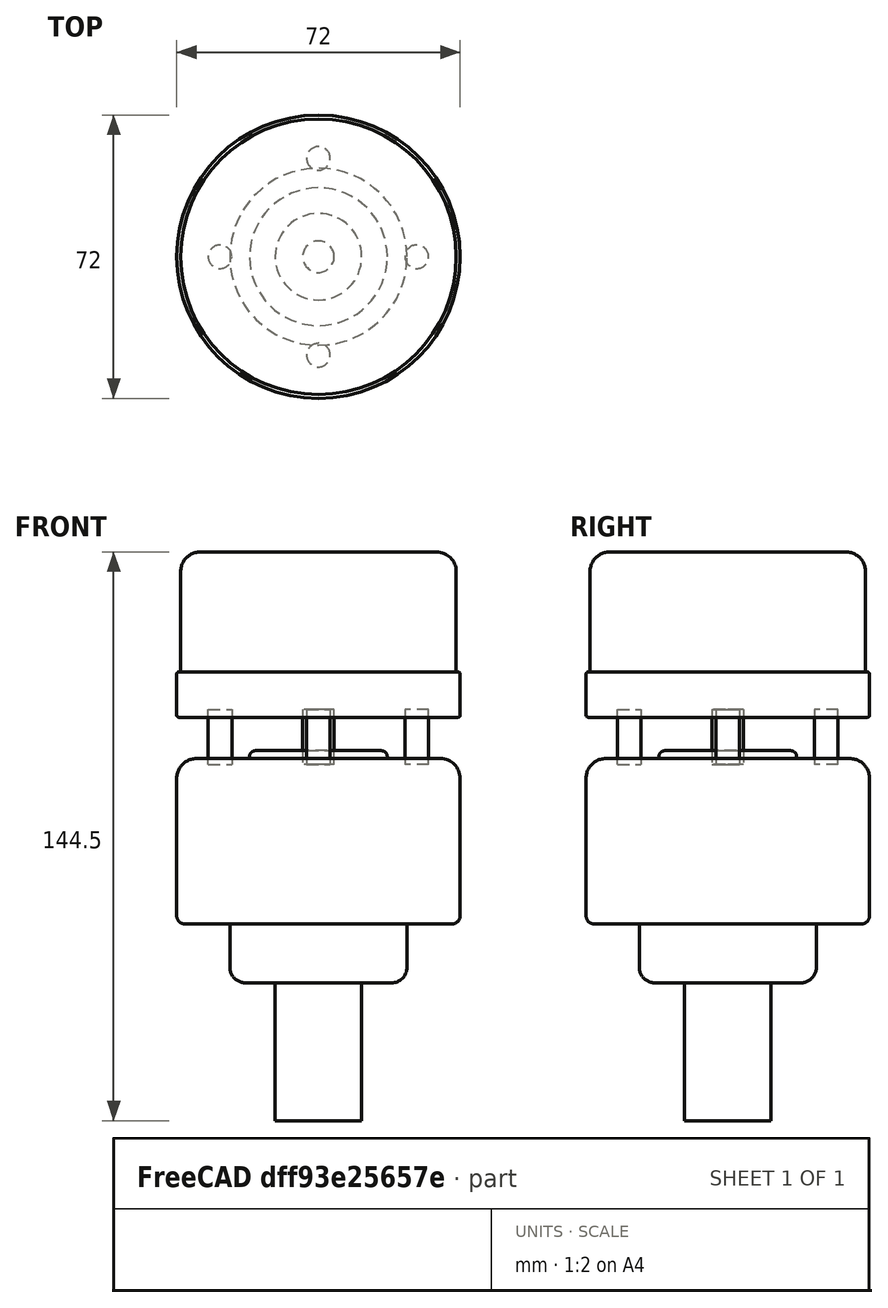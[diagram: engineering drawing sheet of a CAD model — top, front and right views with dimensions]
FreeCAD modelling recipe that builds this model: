
FCSTD DOCUMENT  (FreeCAD 0.21R33668 +7 (Git))
Label: Airmar
License: All rights reserved
LicenseURL: https://en.wikipedia.org/wiki/All_rights_reserved
objects: Part::Cylinder×16, Part::MultiFuse×8, Part::Fillet×5, Part::Mirroring×4, Part::Cut×1
note: 34 computed .brp shape members not serialized (recipe doc carries the construction recipe); baked Part::Feature solids carry a one-line shape summary decoded from their .brp

FEATURE [Part::Cylinder] Cylinder  label="Upper"
  Angle = 360
  AttacherType = Attacher::AttachEngine3D
  FirstAngle = 0
  Height = 42
  Radius = 35
  SecondAngle = 0
FEATURE [Part::Cylinder] Cylinder001  label="Lower"
  Angle = 360
  AttacherType = Attacher::AttachEngine3D
  FirstAngle = 0
  Height = 42
  Placement = pos=(0,0,-52.5) rot=(0,0,1;0rad)
  Radius = 36
  SecondAngle = 0
FEATURE [Part::Cylinder] Cylinder002  label="Cap"
  Angle = 360
  AttacherType = Attacher::AttachEngine3D
  FirstAngle = 0
  Height = 15
  Placement = pos=(0,0,-67.5) rot=(0,0,1;0rad)
  Radius = 22.5
  SecondAngle = 0
FEATURE [Part::Cylinder] Cylinder003  label="Mount"
  Angle = 360
  AttacherType = Attacher::AttachEngine3D
  FirstAngle = 0
  Height = 35
  Placement = pos=(0,0,-102.5) rot=(0,0,1;0rad)
  Radius = 11
  SecondAngle = 0
FEATURE [Part::Cylinder] Cylinder004  label="Cylinder1"
  Angle = 360
  AttacherType = Attacher::AttachEngine3D
  FirstAngle = 0
  Height = 14
  Placement = pos=(25,0,-12) rot=(0,0,1;0rad)
  Radius = 3
  SecondAngle = 0
FEATURE [Part::Cylinder] Cylinder005  label="Cylinder2"
  Angle = 360
  AttacherType = Attacher::AttachEngine3D
  FirstAngle = 0
  Height = 14
  Placement = pos=(25,0,-12) rot=(0,0,1;0rad)
  Radius = 3
  SecondAngle = 0
FEATURE [Part::Mirroring] Part__Mirroring  label="Cylinder2 (Mirror #1)"
  Base = (0,0,0)
  Normal = (1,0,0)
  Source = -> Cylinder005
FEATURE [Part::MultiFuse] Fusion  label="2cyl"
  Shapes = -> [Cylinder004,Part__Mirroring]
FEATURE [Part::Cylinder] Cylinder006
  Angle = 360
  AttacherType = Attacher::AttachEngine3D
  FirstAngle = 0
  Height = 14
  Placement = pos=(25,0,-12) rot=(0,0,1;0rad)
  Radius = 3
  SecondAngle = 0
FEATURE [Part::Cylinder] Cylinder007
  Angle = 360
  AttacherType = Attacher::AttachEngine3D
  FirstAngle = 0
  Height = 14
  Placement = pos=(25,0,-12) rot=(0,0,1;0rad)
  Radius = 3
  SecondAngle = 0
FEATURE [Part::Mirroring] Part__Mirroring001  label="Cylinder2 (Mirror #1)001"
  Base = (0,0,0)
  Normal = (1,0,0)
  Source = -> Cylinder007
FEATURE [Part::MultiFuse] Fusion001  label="2cyl001"
  Placement = pos=(0,0,0) rot=(0,0,1;1.5708rad)
  Shapes = -> [Cylinder006,Part__Mirroring001]
FEATURE [Part::MultiFuse] Fusion002
  Shapes = -> [Fusion,Fusion001]
FEATURE [Part::Cylinder] Cylinder008  label="MiddleCyl"
  Angle = 360
  AttacherType = Attacher::AttachEngine3D
  FirstAngle = 0
  Height = 14
  Placement = pos=(0,0,-12) rot=(0,0,1;0rad)
  Radius = 4
  SecondAngle = 0
FEATURE [Part::Cylinder] Cylinder009 .. Cylinder012  x4 (patterned run collapsed; names and placements below)
  Angle = 360
  AttacherType = Attacher::AttachEngine3D
  FirstAngle = 0
  Height = 2
  Radius = 8.5
  SecondAngle = 0
  placements: all 4 at pos=(20,0,-12) rot=(0,0,1;0rad)
FEATURE [Part::Mirroring] Part__Mirroring002  label="Cylinder2 (Mirror #1)002"
  Base = (0,0,0)
  Normal = (1,0,0)
  Source = -> Cylinder010
FEATURE [Part::MultiFuse] Fusion003  label="2cyl002"
  Shapes = -> [Cylinder009,Part__Mirroring002]
FEATURE [Part::Mirroring] Part__Mirroring003  label="Cylinder2 (Mirror #1)003"
  Base = (0,0,0)
  Normal = (1,0,0)
  Source = -> Cylinder012
FEATURE [Part::MultiFuse] Fusion004  label="2cyl003"
  Placement = pos=(0,0,0) rot=(0,0,1;1.5708rad)
  Shapes = -> [Cylinder011,Part__Mirroring003]
FEATURE [Part::MultiFuse] Fusion005  label="inside_holes"
  Placement = pos=(0,0,12) rot=(0,0,1;0.785398rad)
  Shapes = -> [Fusion003,Fusion004]
FEATURE [Part::Cut] Cut
  Base = -> Cylinder
  Tool = -> Fusion005
FEATURE [Part::Cylinder] Cylinder013  label="mid"
  Angle = 360
  AttacherType = Attacher::AttachEngine3D
  FirstAngle = 0
  Height = 2
  Placement = pos=(0,0,-10.5) rot=(0,0,1;0rad)
  Radius = 17.5
  SecondAngle = 0
FEATURE [Part::Fillet] Fillet
  Base = -> Cut
  Edges = 1 edges r=5: [Edge3]
FEATURE [Part::Cylinder] Cylinder014  label="outer_bot"
  Angle = 360
  AttacherType = Attacher::AttachEngine3D
  FirstAngle = 0
  Height = 6
  Radius = 36
  SecondAngle = 0
FEATURE [Part::Cylinder] Cylinder015  label="outer_top"
  Angle = 360
  AttacherType = Attacher::AttachEngine3D
  FirstAngle = 0
  Height = 5.5
  Placement = pos=(0,0,6) rot=(0,0,1;0rad)
  Radius = 36
  SecondAngle = 0
FEATURE [Part::MultiFuse] Fusion006  label="Outer"
  Shapes = -> [Cylinder014,Cylinder015]
FEATURE [Part::Fillet] Fillet002  label="Bottom"
  Base = -> Cylinder001
  Edges = 2 edges: [Edge2 r=2,Edge3 r=5]
FEATURE [Part::Fillet] Fillet003  label="Mid"
  Base = -> Cylinder013
  Edges = 1 edges r=1.5: [Edge3]
FEATURE [Part::Fillet] Fillet004  label="Cap001"
  Base = -> Cylinder002
  Edges = 1 edges r=4: [Edge2]
FEATURE [Part::MultiFuse] Fusion007  label="upper"
  Shapes = -> [Fillet,Fusion006]
FEATURE [Part::Fillet] Fillet001  label="Upper001"
  Base = -> Fusion007
  Edges = 2 edges r=0.5: [Edge6,Edge10]
